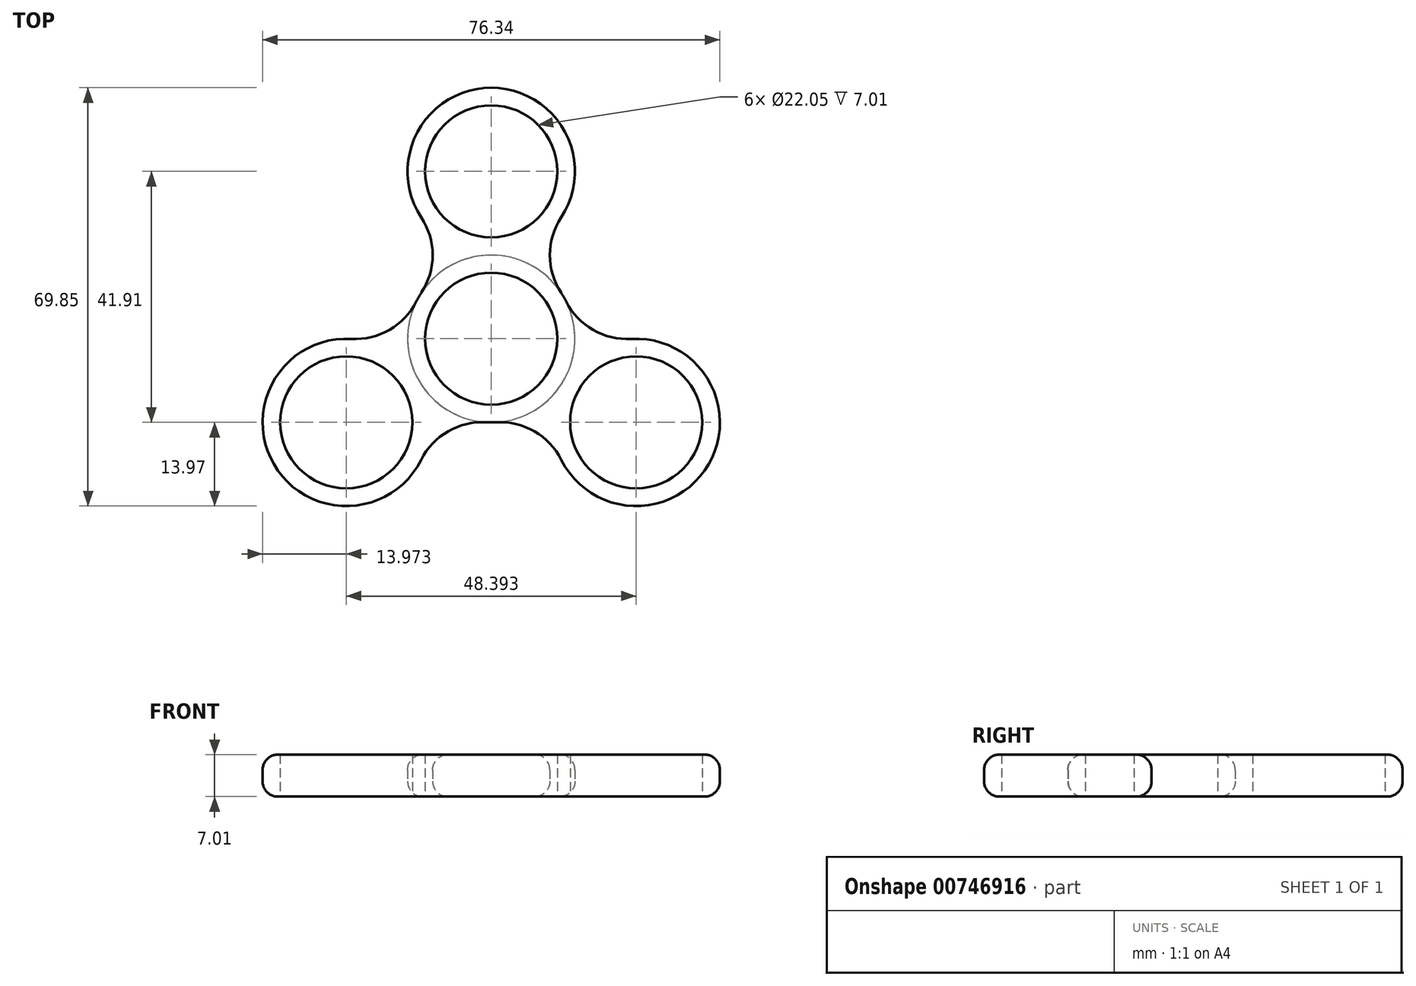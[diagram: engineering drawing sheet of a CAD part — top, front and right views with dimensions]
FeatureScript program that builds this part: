
annotation { "Feature Type Name" : "Feature", "Feature Type Description" : "" }
export const myFeature = defineFeature(function(context is Context, id is Id, definition is map)
    precondition{}
    {
        {
            var Q0;
            Q0=qCreatedBy(makeId("Top.planeOp"),FACE);
            var sketch = newSketch(context, id + "F0", { "sketchPlane" : qUnion([Q0])});
            skCircle(sketch, "E0", {"center": v(0, 0) * mm, "radius": 11.02 * mm});
            skCircle(sketch, "E1", {"center": v(0, 27.94) * mm, "radius": 11.02 * mm});
            skCircle(sketch, "E2", {"center": v(0, 27.94) * mm, "radius": 13.97 * mm});
            skCircle(sketch, "E3", {"center": v(0, 0) * mm, "radius": 13.97 * mm});
            skLineSegment(sketch, "E4.bottom", {"start": v(-13.97, 27.94) * mm, "end": v(13.97, 27.94) * mm});
            skLineSegment(sketch, "E4.top", {"start": v(-13.97, 0) * mm, "end": v(13.97, 0) * mm});
            skLineSegment(sketch, "E4.left", {"start": v(-13.97, 27.94) * mm, "end": v(-13.97, 0) * mm});
            skLineSegment(sketch, "E4.right", {"start": v(13.97, 27.94) * mm, "end": v(13.97, 0) * mm});
            skCircle(sketch, "E5", {"center": v(-21.21, 13.97) * mm, "radius": 11.43 * mm});
            skCircle(sketch, "E6", {"center": v(21.21, 13.97) * mm, "radius": 11.43 * mm});
            skSolve(sketch);
        }
        {
            var Q0;
            {var subQ0=sQuery(id+"F0.wireOp",EDGE,"E4.bottom");var subQ1=sQuery(id+"F0.wireOp",EDGE,"E1");var subQ2=makeQuery(id+"F0.imprint","INTERSECT",VERTEX,{"disambiguationData":[OD(0.0)],"derivedFrom":[subQ1,subQ0]});Q0=makeQuery(id+"F0.imprint","IMPRINT",FACE,{"disambiguationData":[TD([[makeQuery(id+"F0.imprint","IMPRINT",EDGE,{"disambiguationData":[TD([[subQ2,1.0]])],"derivedFrom":subQ1}),-1.0]])]});}
            var Q1;
            {var subQ4=sQuery(id+"F0.wireOp",EDGE,"E4.bottom");var subQ7=sQuery(id+"F0.wireOp",EDGE,"E1");var subQ9=makeQuery(id+"F0.imprint","INTERSECT",VERTEX,{"disambiguationData":[OD(0.0)],"derivedFrom":[subQ7,subQ4]});Q1=makeQuery(id+"F0.imprint","IMPRINT",FACE,{"disambiguationData":[TD([[makeQuery(id+"F0.imprint","IMPRINT",EDGE,{"disambiguationData":[TD([[subQ9,-1.0]])],"derivedFrom":subQ7}),-1.0]])]});}
            var Q2;
            {var subQ0=sQuery(id+"F0.wireOp",EDGE,"E3");var subQ1=sQuery(id+"F0.wireOp",EDGE,"E2");var subQ2=makeQuery(id+"F0.imprint","INTERSECT",VERTEX,{"derivedFrom":[subQ1,subQ0]});Q2=makeQuery(id+"F0.imprint","IMPRINT",FACE,{"disambiguationData":[TD([[makeQuery(id+"F0.imprint","IMPRINT",EDGE,{"disambiguationData":[TD([[subQ2,-1.0]])],"derivedFrom":subQ1}),-1.0]])]});}
            var Q3;
            {var subQ0=sQuery(id+"F0.wireOp",EDGE,"E5");var subQ1=sQuery(id+"F0.wireOp",EDGE,"E2");var subQ2=makeQuery(id+"F0.imprint","INTERSECT",VERTEX,{"derivedFrom":[subQ1,subQ0]});Q3=makeQuery(id+"F0.imprint","IMPRINT",FACE,{"disambiguationData":[TD([[makeQuery(id+"F0.imprint","IMPRINT",EDGE,{"disambiguationData":[TD([[subQ2,-1.0]])],"derivedFrom":subQ1}),-1.0]])]});}
            var Q4;
            {var subQ3=sQuery(id+"F0.wireOp",EDGE,"E4.top");var subQ4=sQuery(id+"F0.wireOp",EDGE,"E0");var subQ5=makeQuery(id+"F0.imprint","INTERSECT",VERTEX,{"disambiguationData":[OD(0.0)],"derivedFrom":[subQ4,subQ3]});Q4=makeQuery(id+"F0.imprint","IMPRINT",FACE,{"disambiguationData":[TD([[makeQuery(id+"F0.imprint","IMPRINT",EDGE,{"disambiguationData":[TD([[subQ5,1.0]])],"derivedFrom":subQ4}),-1.0]])]});}
            var Q5;
            {var subQ0=sQuery(id+"F0.wireOp",EDGE,"E4.top");var subQ1=sQuery(id+"F0.wireOp",EDGE,"E0");var subQ2=makeQuery(id+"F0.imprint","INTERSECT",VERTEX,{"disambiguationData":[OD(0.0)],"derivedFrom":[subQ1,subQ0]});Q5=makeQuery(id+"F0.imprint","IMPRINT",FACE,{"disambiguationData":[TD([[makeQuery(id+"F0.imprint","IMPRINT",EDGE,{"disambiguationData":[TD([[subQ2,-1.0]])],"derivedFrom":subQ1}),-1.0]])]});}
            extrude(context, id + "F1", {"entities" : qUnion([Q0, Q1, Q2, Q3, Q4, Q5]), "depth" : 7 * mm, "offsetDistance" : 25.4 * mm});
        }
        {
            var Q0;
            Q0=qCreatedBy(makeId("Top.planeOp"),FACE);
            var sketch = newSketch(context, id + "F2", { "sketchPlane" : qUnion([Q0])});
            skCircle(sketch, "E7", {"center": v(0, 0) * mm, "radius": 5.8 * mm});
            skSolve(sketch);
        }
        {
            var Q0;
            Q0=makeQuery(id+"F1.opExtrude","SWEPT_BODY",BODY,{"disambiguationData":[OSD([sQuery(id+"F0.wireOp",EDGE,"E0"),sQuery(id+"F0.wireOp",EDGE,"E1"),sQuery(id+"F0.wireOp",EDGE,"E2"),sQuery(id+"F0.wireOp",EDGE,"E3"),sQuery(id+"F0.wireOp",EDGE,"E5"),sQuery(id+"F0.wireOp",EDGE,"E6")])]});
            var Q1;
            Q1=sQuery(id+"F2.wireOp",EDGE,"E7");
            circularPattern(context, id + "F3", {"entities" : qUnion([Q0]), "axis" : qUnion([Q1]), "angle" : 360 * degree, "instanceCount" : 3, "equalSpace" : true});
        }
        {
            var Q0;
            Q0=makeQuery(id+"F3.opPattern","COPY",EDGE,{"derivedFrom":makeQuery(id+"F1.opExtrude","CAP_EDGE",EDGE,{"disambiguationData":[OSD([sQuery(id+"F0.wireOp",EDGE,"E2")])],"isStart":false}),"instanceName":"1"});
            var Q1;
            Q1=makeQuery(id+"F3.opPattern","COPY",EDGE,{"derivedFrom":makeQuery(id+"F1.opExtrude","CAP_EDGE",EDGE,{"disambiguationData":[OSD([sQuery(id+"F0.wireOp",EDGE,"E2")])],"isStart":false}),"instanceName":"2"});
            var Q2;
            Q2=makeQuery(id+"F1.opExtrude","CAP_EDGE",EDGE,{"disambiguationData":[OSD([sQuery(id+"F0.wireOp",EDGE,"E2")])],"isStart":false});
            var Q3;
            Q3=makeQuery(id+"F1.opExtrude","CAP_EDGE",EDGE,{"disambiguationData":[OSD([sQuery(id+"F0.wireOp",EDGE,"E2")])],"isStart":true});
            var Q4;
            Q4=makeQuery(id+"F3.opPattern","COPY",EDGE,{"derivedFrom":makeQuery(id+"F1.opExtrude","CAP_EDGE",EDGE,{"disambiguationData":[OSD([sQuery(id+"F0.wireOp",EDGE,"E2")])],"isStart":true}),"instanceName":"1"});
            var Q5;
            Q5=makeQuery(id+"F3.opPattern","COPY",EDGE,{"derivedFrom":makeQuery(id+"F1.opExtrude","CAP_EDGE",EDGE,{"disambiguationData":[OSD([sQuery(id+"F0.wireOp",EDGE,"E2")])],"isStart":true}),"instanceName":"2"});
            fillet(context, id + "F4", {"entities" : qUnion([Q0, Q1, Q2, Q3, Q4, Q5]), "radius" : 2.54 * mm, "tangentPropagation" : true, "allowEdgeOverflow" : false});
        }
    });
